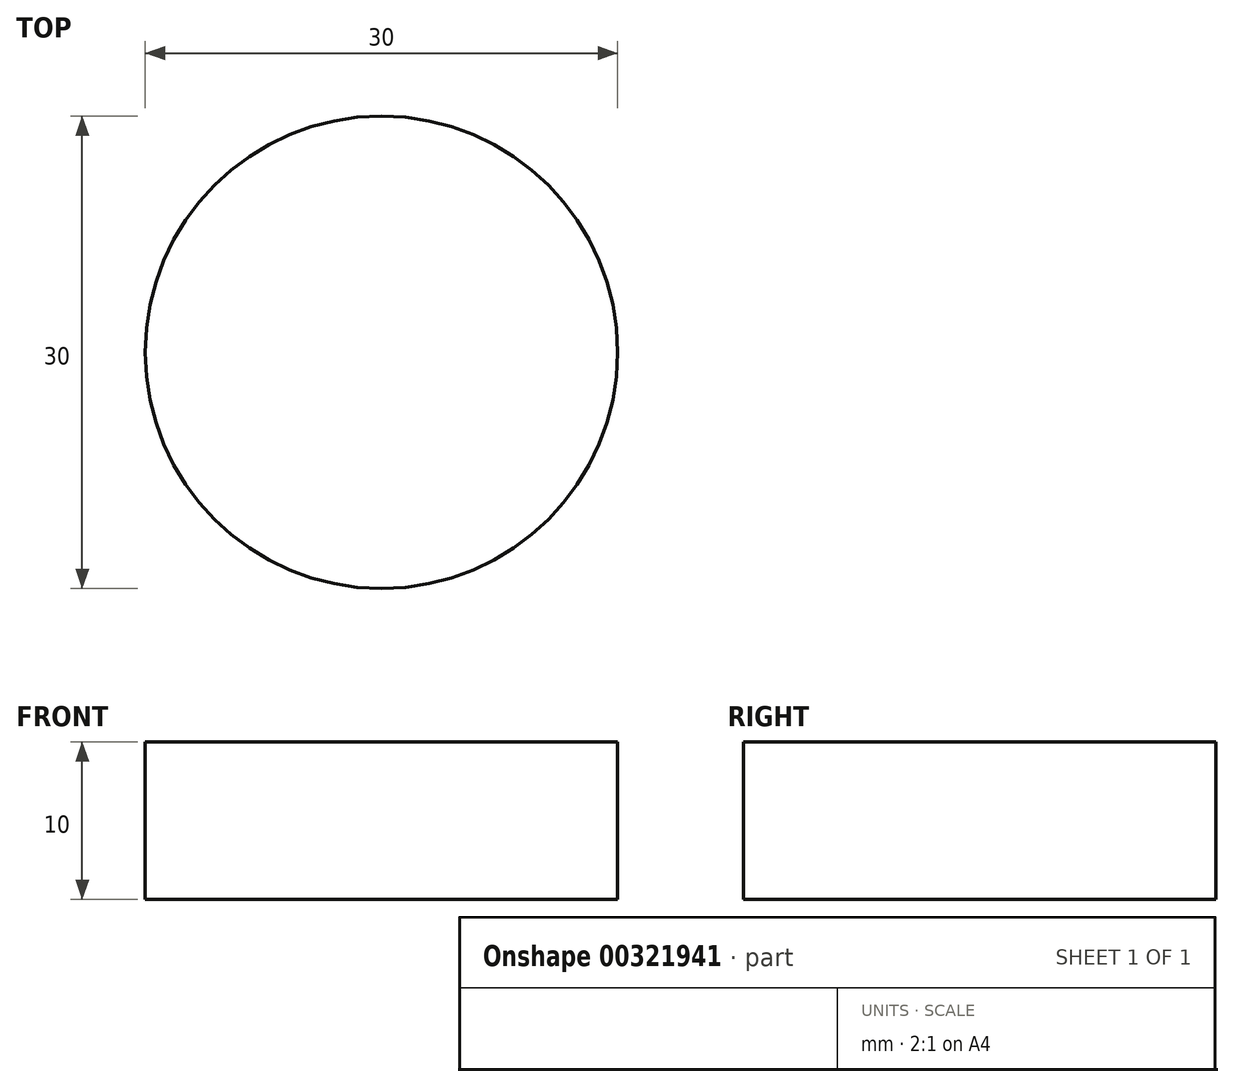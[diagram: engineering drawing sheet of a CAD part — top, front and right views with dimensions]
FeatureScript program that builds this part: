
annotation { "Feature Type Name" : "Feature", "Feature Type Description" : "" }
export const myFeature = defineFeature(function(context is Context, id is Id, definition is map)
    precondition{}
    {
        {
            var Q0;
            Q0=qCreatedBy(makeId("Top.planeOp"),FACE);
            var sketch = newSketch(context, id + "F0", { "sketchPlane" : qUnion([Q0])});
            skCircle(sketch, "E0", {"center": v(0, 0) * mm, "radius": 15 * mm});
            skSolve(sketch);
        }
        {
            var Q0;
            Q0 = qSketchRegion(id + "F0", true);
            extrude(context, id + "F1", {"entities" : qUnion([Q0]), "endBound" : BoundingType.SYMMETRIC, "depth" : 10 * mm});
        }
    });
